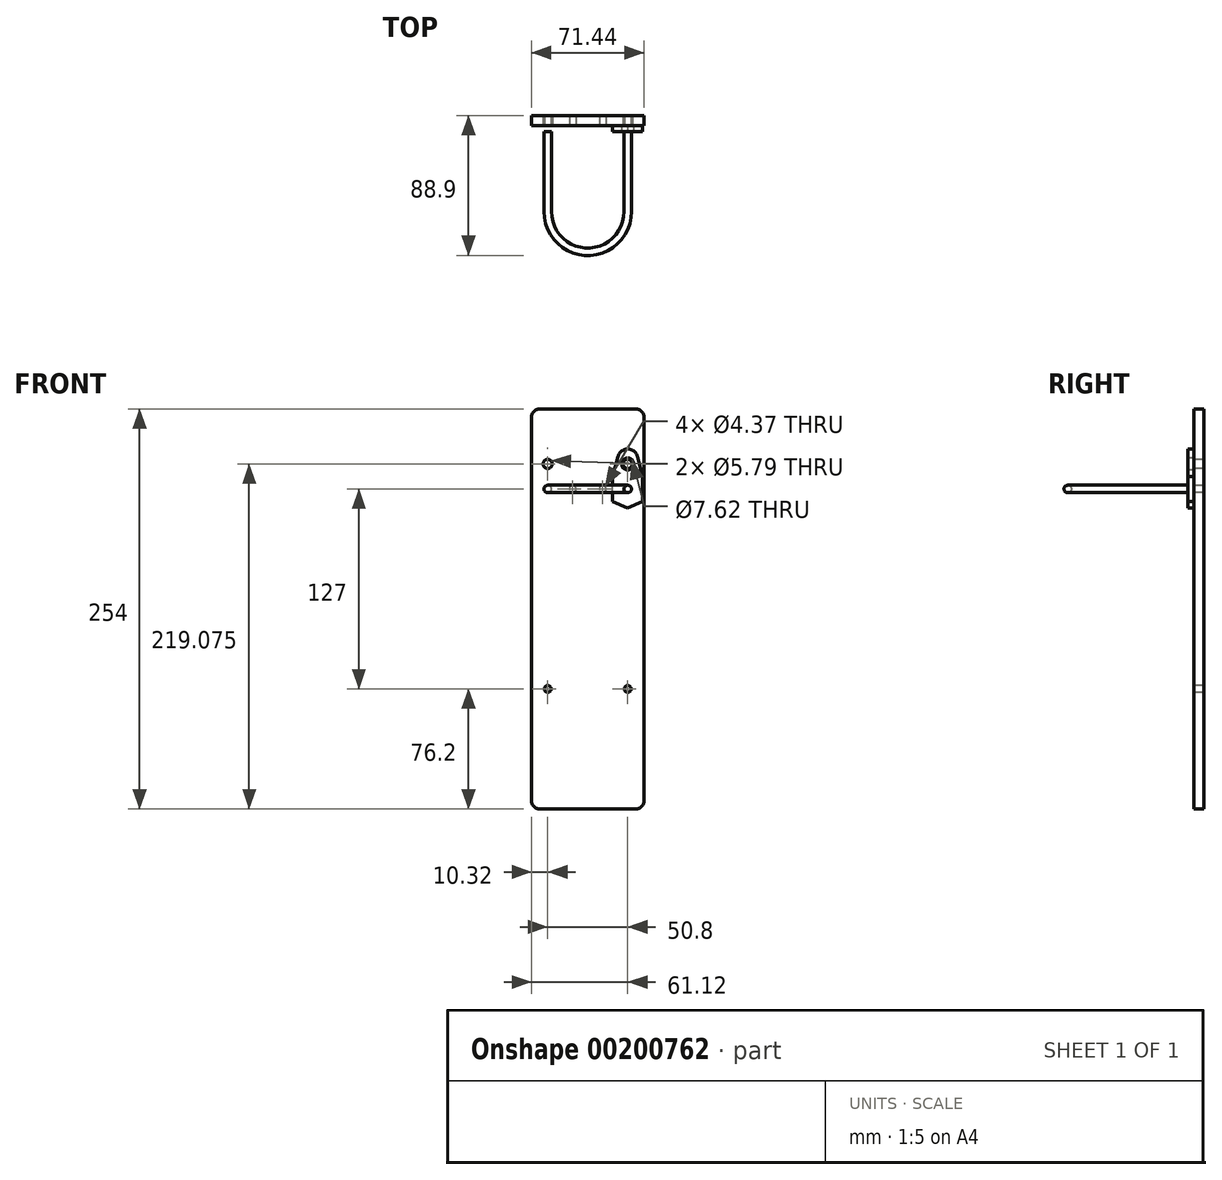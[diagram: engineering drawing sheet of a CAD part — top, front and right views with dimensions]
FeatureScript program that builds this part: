
annotation { "Feature Type Name" : "Feature", "Feature Type Description" : "" }
export const myFeature = defineFeature(function(context is Context, id is Id, definition is map)
    precondition{}
    {
        {
            var Q0;
            Q0=qCreatedBy(makeId("Front.planeOp"),FACE);
            var sketch = newSketch(context, id + "F0", { "sketchPlane" : qUnion([Q0])});
            skCircle(sketch, "E0", {"center": v(-25.4, 0) * mm, "radius": 2.38 * mm});
            skLineSegment(sketch, "E1", {"start": v(-25.4, 0) * mm, "end": v(0, 0) * mm, "construction": true});
            skLineSegment(sketch, "E2", {"start": v(0, 0) * mm, "end": v(25.4, 0) * mm, "construction": true});
            skLineSegment(sketch, "E3", {"start": v(0, 0) * mm, "end": v(0, 43.45) * mm, "construction": true});
            skSolve(sketch);
        }
        {
            var Q0;
            Q0=qCreatedBy(makeId("Top.planeOp"),FACE);
            var sketch = newSketch(context, id + "F1", { "sketchPlane" : qUnion([Q0])});
            skArc(sketch, "E4", {"start": v(-25.4, -50.8) * mm, "mid": v(0, -76.2) * mm, "end": v(25.4, -50.8) * mm});
            skLineSegment(sketch, "E5", {"start": v(-25.4, -50.8) * mm, "end": v(-25.4, 0) * mm});
            skLineSegment(sketch, "E6", {"start": v(25.4, -50.8) * mm, "end": v(25.4, 0) * mm});
            skLineSegment(sketch, "E7", {"start": v(-28.33, -76.2) * mm, "end": v(33.13, -76.2) * mm, "construction": true});
            skSolve(sketch);
        }
        {
            var Q0;
            Q0=makeQuery(id+"F0.imprint","IMPRINT",FACE,{"disambiguationData":[TD([[makeQuery(id+"F0.imprint","IMPRINT",EDGE,{"derivedFrom":sQuery(id+"F0.wireOp",EDGE,"E0")}),1.0]])]});
            var Q1;
            Q1=sQuery(id+"F1.wireOp",EDGE,"E5");
            var Q2;
            Q2=sQuery(id+"F1.wireOp",EDGE,"E4");
            var Q3;
            Q3=sQuery(id+"F1.wireOp",EDGE,"E6");
            sweep(context, id + "F2", {"profiles" : qUnion([Q0]), "path" : qUnion([Q1, Q2, Q3])});
        }
        {
            var Q0;
            Q0=qCreatedBy(makeId("Front.planeOp"),FACE);
            var sketch = newSketch(context, id + "F3", { "sketchPlane" : qUnion([Q0])});
            skCircle(sketch, "E8", {"center": v(25.4, 15.88) * mm, "radius": 3.81 * mm});
            skLineSegment(sketch, "E9", {"start": v(31.54, 20.68) * mm, "end": v(34.92, 7.94) * mm});
            skLineSegment(sketch, "E10", {"start": v(34.93, 7.94) * mm, "end": v(34.93, -7.94) * mm});
            skLineSegment(sketch, "E11", {"start": v(34.93, -7.94) * mm, "end": v(25.4, -12.17) * mm});
            skLineSegment(sketch, "E12", {"start": v(25.4, -12.17) * mm, "end": v(15.88, -7.94) * mm});
            skLineSegment(sketch, "E13", {"start": v(15.88, -7.94) * mm, "end": v(15.88, 7.94) * mm});
            skLineSegment(sketch, "E14", {"start": v(15.88, 7.94) * mm, "end": v(19.26, 20.68) * mm});
            skLineSegment(sketch, "E15", {"start": v(25.4, -12.17) * mm, "end": v(25.4, 15.88) * mm, "construction": true});
            skLineSegment(sketch, "E16", {"start": v(34.93, -7.94) * mm, "end": v(25.4, -7.94) * mm, "construction": true});
            skLineSegment(sketch, "E17", {"start": v(25.4, -7.94) * mm, "end": v(15.88, -7.94) * mm, "construction": true});
            skArc(sketch, "E18", {"start": v(31.54, 20.68) * mm, "mid": v(25.4, 25.4) * mm, "end": v(19.26, 20.68) * mm});
            skLineSegment(sketch, "E19", {"start": v(27.78, -11.11) * mm, "end": v(23.02, -11.11) * mm, "construction": true});
            skSolve(sketch);
        }
        {
            var Q0;
            Q0 = qSketchRegion(id + "F3", true);
            extrude(context, id + "F4", {"entities" : qUnion([Q0]), "operationType" : NewBodyOperationType.ADD, "flatOperationType" : FlatOperationType.REMOVE, "oppositeDirection" : true, "offsetDistance" : 25.4 * mm, "depth" : 3.97 * mm, "domain" : OperationDomain.MODEL});
        }
        {
            var Q0;
            Q0=makeQuery(id+"F4.opExtrude","CAP_FACE",FACE,{"disambiguationData":[OSD([sQuery(id+"F3.wireOp",EDGE,"E8"),sQuery(id+"F3.wireOp",EDGE,"E9"),sQuery(id+"F3.wireOp",EDGE,"E10"),sQuery(id+"F3.wireOp",EDGE,"E11"),sQuery(id+"F3.wireOp",EDGE,"E12"),sQuery(id+"F3.wireOp",EDGE,"E13"),sQuery(id+"F3.wireOp",EDGE,"E14"),sQuery(id+"F3.wireOp",EDGE,"E18")])],"isStart":false});
            var sketch = newSketch(context, id + "F5", { "sketchPlane" : qUnion([Q0])});
            skLineSegment(sketch, "E20.bottom", {"start": v(35.72, 50.8) * mm, "end": v(-35.72, 50.8) * mm});
            skLineSegment(sketch, "E20.top", {"start": v(35.72, -203.2) * mm, "end": v(-35.72, -203.2) * mm});
            skLineSegment(sketch, "E20.left", {"start": v(35.72, 50.8) * mm, "end": v(35.72, -203.2) * mm});
            skLineSegment(sketch, "E20.right", {"start": v(-35.72, 50.8) * mm, "end": v(-35.72, -203.2) * mm});
            skPoint(sketch, "E20.middle", {"position": v(0, -76.2) * mm});
            skCircle(sketch, "E21", {"center": v(-25.4, 15.88) * mm, "radius": 2.9 * mm});
            skCircle(sketch, "E22", {"center": v(25.4, 15.88) * mm, "radius": 2.9 * mm});
            skCircle(sketch, "E23", {"center": v(9.53, 0) * mm, "radius": 2.18 * mm});
            skLineSegment(sketch, "E24", {"start": v(0, 0) * mm, "end": v(0, 21.66) * mm, "construction": true});
            skCircle(sketch, "E25.MirrorC", {"center": v(-9.53, 0) * mm, "radius": 2.18 * mm});
            skCircle(sketch, "E26", {"center": v(25.4, -127) * mm, "radius": 4.76 * mm, "construction": true});
            skLineSegment(sketch, "E27", {"start": v(0, -76.2) * mm, "end": v(0, -145.21) * mm, "construction": true});
            skCircle(sketch, "E28", {"center": v(25.4, -127) * mm, "radius": 2.18 * mm});
            skCircle(sketch, "E29.MirrorC", {"center": v(-25.4, -127) * mm, "radius": 2.18 * mm});
            skCircle(sketch, "E30.MirrorC", {"center": v(-25.4, -127) * mm, "radius": 4.76 * mm, "construction": true});
            skSolve(sketch);
        }
        {
            var Q0;
            Q0 = qSketchRegion(id + "F5", true);
            extrude(context, id + "F6", {"entities" : qUnion([Q0]), "depth" : 6.35 * mm});
        }
        {
            var Q0;
            Q0=makeQuery(id+"F6.opExtrude","SWEPT_EDGE",EDGE,{"disambiguationData":[OSD([sQuery(id+"F5.wireOp",EDGE,"E20.bottom"),sQuery(id+"F5.wireOp",EDGE,"E20.left")])]});
            var Q1;
            Q1=makeQuery(id+"F6.opExtrude","SWEPT_EDGE",EDGE,{"disambiguationData":[OSD([sQuery(id+"F5.wireOp",EDGE,"E20.bottom"),sQuery(id+"F5.wireOp",EDGE,"E20.right")])]});
            var Q2;
            Q2=makeQuery(id+"F6.opExtrude","SWEPT_EDGE",EDGE,{"disambiguationData":[OSD([sQuery(id+"F5.wireOp",EDGE,"E20.top"),sQuery(id+"F5.wireOp",EDGE,"E20.right")])]});
            var Q3;
            Q3=makeQuery(id+"F6.opExtrude","SWEPT_EDGE",EDGE,{"disambiguationData":[OSD([sQuery(id+"F5.wireOp",EDGE,"E20.top"),sQuery(id+"F5.wireOp",EDGE,"E20.left")])]});
            fillet(context, id + "F7", {"entities" : qUnion([Q0, Q1, Q2, Q3]), "radius" : 5.08 * mm, "tangentPropagation" : true, "allowEdgeOverflow" : false});
        }
    });
